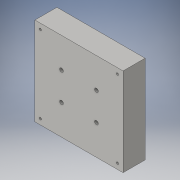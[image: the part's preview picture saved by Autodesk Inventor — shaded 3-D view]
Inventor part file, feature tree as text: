
AUTODESK INVENTOR PART (.ipt)
format: ipt  version: 2016 (Build 200138000, 138)  size: 129,024 bytes
history: native  units: in
note: dims shown in document units (in); Inventor stores cm internally (conversion verified against a paired STEP export)
features: sketch x3, hole x2, extrude x1
ambient origin geometry x8: Origin, YZ Plane, XZ Plane, XY Plane, X Axis, Y Axis, Z Axis, Center Point
bodies: Solid1 (feature_tree)
feature tree (6):
  extrude  "Extrusion1"  Depth=3.1496in
  hole  "Hole1"  [1 undecoded]
  hole  "Hole2"  [1 undecoded]
  sketch  "Sketch2"  dims[d0=3.1496in d1=3.1496in]
  sketch  "Sketch3"  dims[d2=0.7874in d3=0.0in d4=0.0984in]
  sketch  "Sketch4"  dims[d5=0.1969in d6=0.1969in d7=0.1969in d8=0.1969in d9=0.0984in d10=0.1969in d11=0.1969in d12=0.0984in d13=0.0793in d14=0.1969in d15=0.1575in d16=0.0787in d17=90.0deg d18=0.2992in d19=0.8108in d20=0.9498in d21=0.9498in d22=1.0748in d23=1.0748in d24=1.25in d25=1.25in d26=1.0in d27=1.0in d28=0.1181in d29=0.1181in d30=0.1181in d31=0.1181in d32=0.1339in d33=0.2362in d34=0.2362in d35=0.1969in d36=90.0deg d37=0.3465in d38=0.8108in d39=0.1969in d40=0.1969in]
note: 2 required parameter values undecoded (feature->parameter linkage not recoverable at this tier; creation-order binding heuristic only, values carry confidence <= 0.55)
